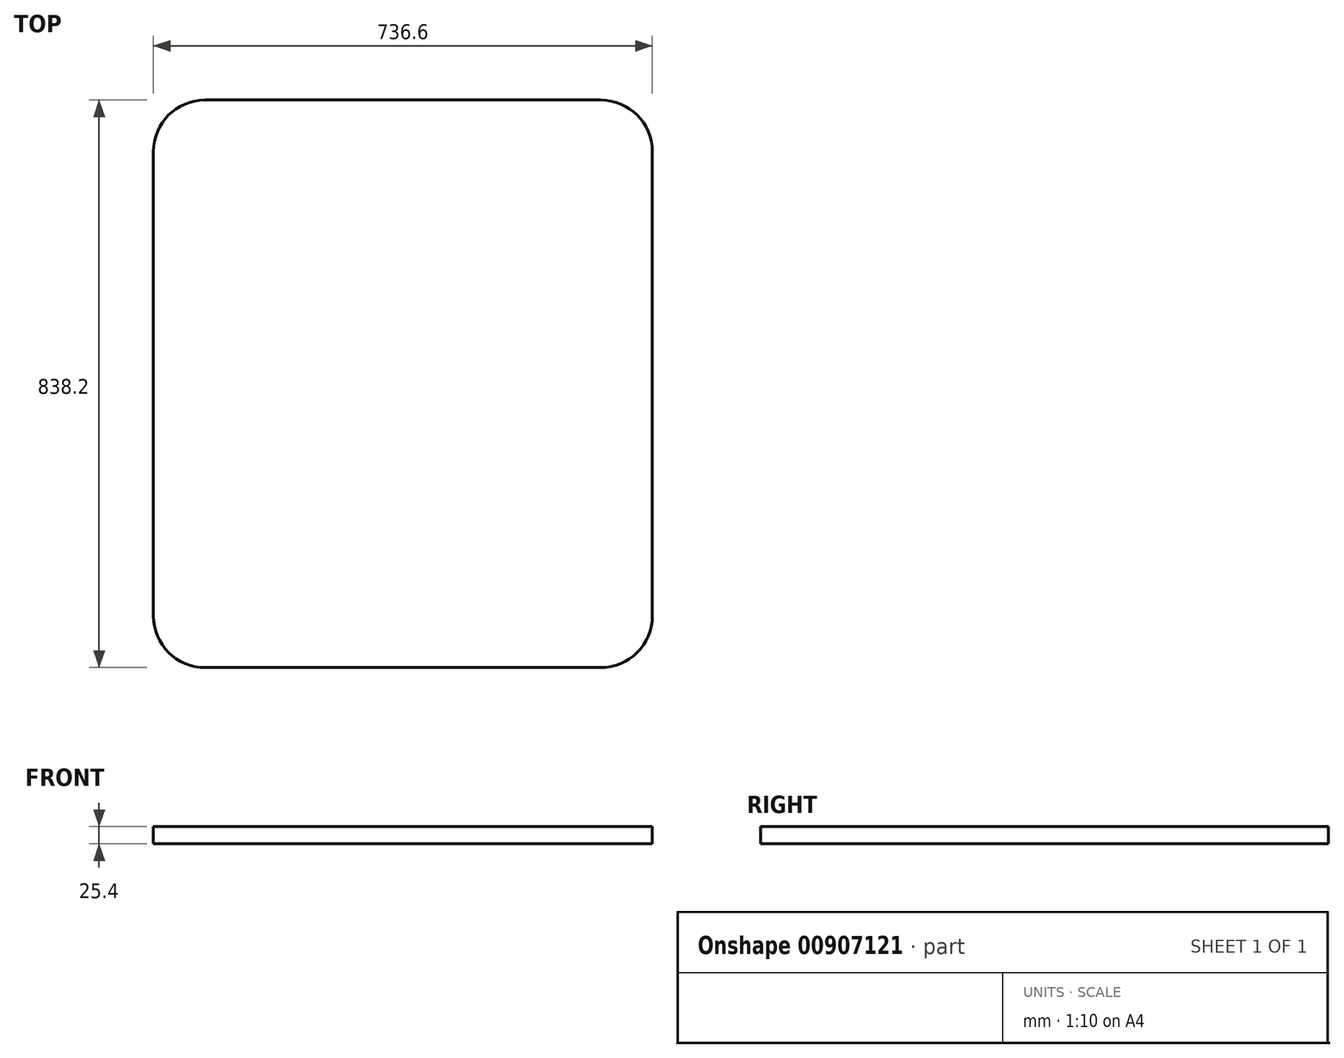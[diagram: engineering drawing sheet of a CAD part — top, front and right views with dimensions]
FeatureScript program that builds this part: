
annotation { "Feature Type Name" : "Feature", "Feature Type Description" : "" }
export const myFeature = defineFeature(function(context is Context, id is Id, definition is map)
    precondition{}
    {
        {
            var Q0;
            Q0=qCreatedBy(makeId("Top.planeOp"),FACE);
            var sketch = newSketch(context, id + "F0", { "sketchPlane" : qUnion([Q0])});
            skLineSegment(sketch, "E0.bottom", {"start": v(-298.73, 591.34) * mm, "end": v(285.47, 591.34) * mm});
            skLineSegment(sketch, "E0.top", {"start": v(-298.73, -246.86) * mm, "end": v(285.47, -246.86) * mm});
            skLineSegment(sketch, "E0.left", {"start": v(-374.93, 515.14) * mm, "end": v(-374.93, -170.66) * mm});
            skLineSegment(sketch, "E0.right", {"start": v(361.67, 515.14) * mm, "end": v(361.67, -170.66) * mm});
            skPoint(sketch, "E1.visualSharp", {"position": v(-374.93, 591.34) * mm});
            skArc(sketch, "E1.filletArc", {"start": v(-298.73, 591.34) * mm, "mid": v(-352.61, 569.02) * mm, "end": v(-374.93, 515.14) * mm});
            skPoint(sketch, "E2.visualSharp", {"position": v(-374.93, -246.86) * mm});
            skArc(sketch, "E2.filletArc", {"start": v(-374.93, -170.66) * mm, "mid": v(-352.61, -224.55) * mm, "end": v(-298.73, -246.86) * mm});
            skPoint(sketch, "E3.visualSharp", {"position": v(361.67, -246.86) * mm});
            skArc(sketch, "E3.filletArc", {"start": v(285.47, -246.86) * mm, "mid": v(339.35, -224.55) * mm, "end": v(361.67, -170.66) * mm});
            skPoint(sketch, "E4.visualSharp", {"position": v(361.67, 591.34) * mm});
            skArc(sketch, "E4.filletArc", {"start": v(361.67, 515.14) * mm, "mid": v(339.35, 569.02) * mm, "end": v(285.47, 591.34) * mm});
            skSolve(sketch);
        }
        {
            var Q0;
            Q0=qSketchRegion(id+"F0",true);
            extrude(context, id + "F1", {"entities" : qUnion([Q0]), "depth" : 25.4 * mm, "offsetDistance" : 25.4 * mm});
        }
    });
